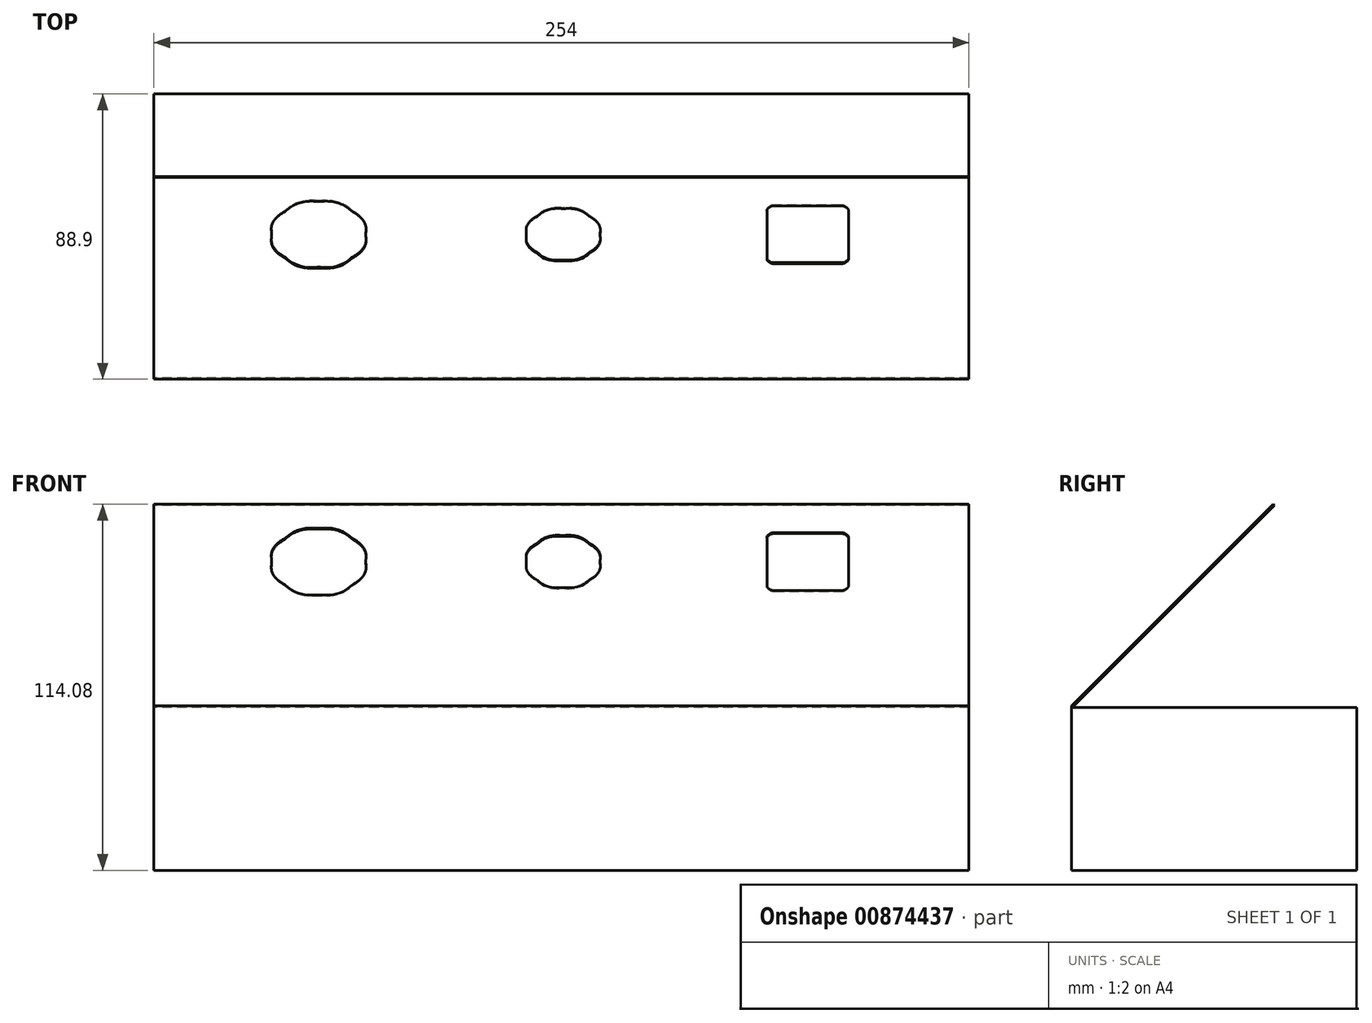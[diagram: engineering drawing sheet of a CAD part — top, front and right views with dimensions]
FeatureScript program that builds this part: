
annotation { "Feature Type Name" : "Feature", "Feature Type Description" : "" }
export const myFeature = defineFeature(function(context is Context, id is Id, definition is map)
    precondition{}
    {
        {
            var Q0;
            Q0=qCreatedBy(makeId("Right.planeOp"),FACE);
            var sketch = newSketch(context, id + "F0", { "sketchPlane" : qUnion([Q0])});
            skLineSegment(sketch, "E0.bottom", {"start": v(0, 0) * mm, "end": v(-88.9, 0) * mm});
            skLineSegment(sketch, "E0.top", {"start": v(0, 50.8) * mm, "end": v(-88.5, 50.8) * mm});
            skLineSegment(sketch, "E0.left", {"start": v(0, 0) * mm, "end": v(0, 50.8) * mm});
            skLineSegment(sketch, "E0.right", {"start": v(-88.9, 0) * mm, "end": v(-88.9, 51.22) * mm});
            skLineSegment(sketch, "E1", {"start": v(-88.9, 51.22) * mm, "end": v(-26.04, 114.08) * mm});
            skLineSegment(sketch, "E2", {"start": v(-26.04, 114.08) * mm, "end": v(-25.75, 113.8) * mm});
            skLineSegment(sketch, "E3", {"start": v(-25.75, 113.8) * mm, "end": v(-88.5, 51.05) * mm});
            skLineSegment(sketch, "E4", {"start": v(-88.5, 50.8) * mm, "end": v(-88.5, 51.05) * mm});
            skLineSegment(sketch, "E5", {"start": v(-88.5, 50.8) * mm, "end": v(-88.9, 50.8) * mm, "construction": true});
            skSolve(sketch);
        }
        {
            var Q0;
            Q0=qSketchRegion(id+"F0",true);
            extrude(context, id + "F1", {"entities" : qUnion([Q0]), "endBound" : BoundingType.SYMMETRIC, "depth" : 254 * mm, "offsetDistance" : 25.4 * mm});
        }
        {
            var Q0;
            Q0=makeQuery(id+"F1.opExtrude","SWEPT_FACE",FACE,{"disambiguationData":[OSD([sQuery(id+"F0.wireOp",EDGE,"E1")])]});
            var sketch = newSketch(context, id + "F2", { "sketchPlane" : qUnion([Q0])});
            skLineSegment(sketch, "E6", {"start": v(89.43, 26.68) * mm, "end": v(89.43, 47.32) * mm});
            skLineSegment(sketch, "E7", {"start": v(87.05, 49.7) * mm, "end": v(66.4, 49.7) * mm});
            skLineSegment(sketch, "E8", {"start": v(66.4, 24.3) * mm, "end": v(87.05, 24.3) * mm});
            skLineSegment(sketch, "E9", {"start": v(64.03, 47.32) * mm, "end": v(64.03, 26.68) * mm});
            skLineSegment(sketch, "E10", {"start": v(127.53, -26.5) * mm, "end": v(127.53, 61.6) * mm, "construction": true});
            skLineSegment(sketch, "E11", {"start": v(-126.47, 61.6) * mm, "end": v(127.53, 61.6) * mm, "construction": true});
            skLineSegment(sketch, "E12", {"start": v(-126.47, -26.5) * mm, "end": v(-126.47, 61.6) * mm, "construction": true});
            skLineSegment(sketch, "E13", {"start": v(127.53, -26.5) * mm, "end": v(-126.47, -26.5) * mm, "construction": true});
            skFitSpline(sketch, "E14", {"points": [v(-75.67, 51.69) * mm, v(-79.52, 51.69) * mm, v(-83.34, 50.1) * mm, v(-86.06, 47.39) * mm]});
            skFitSpline(sketch, "E15", {"points": [v(-86.06, 47.39) * mm, v(-88.77, 44.67) * mm, v(-90.36, 40.85) * mm, v(-90.36, 37) * mm, v(-90.36, 33.16) * mm, v(-88.77, 29.34) * mm, v(-86.06, 26.62) * mm]});
            skFitSpline(sketch, "E16", {"points": [v(-86.06, 26.62) * mm, v(-83.34, 23.9) * mm, v(-79.52, 22.32) * mm, v(-75.67, 22.32) * mm, v(-71.83, 22.32) * mm, v(-68, 23.9) * mm, v(-65.29, 26.62) * mm]});
            skFitSpline(sketch, "E17", {"points": [v(-65.29, 26.62) * mm, v(-62.57, 29.34) * mm, v(-60.99, 33.16) * mm, v(-60.99, 37) * mm, v(-60.99, 40.85) * mm, v(-62.57, 44.67) * mm, v(-65.29, 47.39) * mm]});
            skFitSpline(sketch, "E18", {"points": [v(-65.29, 47.39) * mm, v(-68, 50.1) * mm, v(-71.83, 51.69) * mm, v(-75.67, 51.69) * mm]});
            skFitSpline(sketch, "E19", {"points": [v(89.43, 47.32) * mm, v(89.43, 47.94) * mm, v(89.17, 48.56) * mm, v(88.73, 49) * mm]});
            skFitSpline(sketch, "E20", {"points": [v(88.73, 49) * mm, v(88.29, 49.45) * mm, v(87.67, 49.7) * mm, v(87.05, 49.7) * mm]});
            skFitSpline(sketch, "E21", {"points": [v(87.05, 24.3) * mm, v(87.67, 24.3) * mm, v(88.29, 24.56) * mm, v(88.73, 25) * mm]});
            skFitSpline(sketch, "E22", {"points": [v(88.73, 25) * mm, v(89.17, 25.44) * mm, v(89.43, 26.06) * mm, v(89.43, 26.68) * mm]});
            skFitSpline(sketch, "E23", {"points": [v(64.03, 26.68) * mm, v(64.03, 26.06) * mm, v(64.29, 25.44) * mm, v(64.73, 25) * mm]});
            skFitSpline(sketch, "E24", {"points": [v(64.73, 25) * mm, v(65.17, 24.56) * mm, v(65.79, 24.3) * mm, v(66.4, 24.3) * mm]});
            skFitSpline(sketch, "E25", {"points": [v(66.4, 49.7) * mm, v(65.79, 49.7) * mm, v(65.17, 49.45) * mm, v(64.73, 49) * mm]});
            skFitSpline(sketch, "E26", {"points": [v(64.73, 49) * mm, v(64.29, 48.56) * mm, v(64.03, 47.94) * mm, v(64.03, 47.32) * mm]});
            skFitSpline(sketch, "E27", {"points": [v(0.53, 48.51) * mm, v(-2.49, 48.51) * mm, v(-5.48, 47.27) * mm, v(-7.6, 45.14) * mm]});
            skFitSpline(sketch, "E28", {"points": [v(-7.6, 45.14) * mm, v(-9.74, 43.01) * mm, v(-10.98, 40.02) * mm, v(-10.98, 37) * mm, v(-10.98, 33.99) * mm, v(-9.74, 31) * mm, v(-7.6, 28.86) * mm]});
            skFitSpline(sketch, "E29", {"points": [v(-7.6, 28.86) * mm, v(-5.48, 26.73) * mm, v(-2.49, 25.5) * mm, v(0.53, 25.5) * mm, v(3.54, 25.5) * mm, v(6.54, 26.73) * mm, v(8.67, 28.86) * mm]});
            skFitSpline(sketch, "E30", {"points": [v(8.67, 28.86) * mm, v(10.8, 31) * mm, v(12.04, 33.99) * mm, v(12.04, 37) * mm, v(12.04, 40.02) * mm, v(10.8, 43.01) * mm, v(8.67, 45.14) * mm]});
            skFitSpline(sketch, "E31", {"points": [v(8.67, 45.14) * mm, v(6.54, 47.27) * mm, v(3.54, 48.51) * mm, v(0.53, 48.51) * mm]});
            skFitSpline(sketch, "E32", {"points": [v(0.53, 48.51) * mm, v(-2.49, 48.51) * mm, v(-5.48, 47.27) * mm, v(-7.6, 45.14) * mm]});
            skFitSpline(sketch, "E33", {"points": [v(-7.6, 45.14) * mm, v(-9.74, 43) * mm, v(-10.98, 40.02) * mm, v(-10.98, 37) * mm, v(-10.98, 33.99) * mm, v(-9.74, 31) * mm, v(-7.6, 28.86) * mm]});
            skFitSpline(sketch, "E34", {"points": [v(-7.6, 28.86) * mm, v(-5.48, 26.73) * mm, v(-2.49, 25.5) * mm, v(0.53, 25.5) * mm, v(3.54, 25.5) * mm, v(6.54, 26.73) * mm, v(8.67, 28.86) * mm]});
            skFitSpline(sketch, "E35", {"points": [v(8.67, 28.86) * mm, v(10.8, 31) * mm, v(12.04, 33.99) * mm, v(12.04, 37) * mm, v(12.04, 40.02) * mm, v(10.8, 43) * mm, v(8.67, 45.14) * mm]});
            skFitSpline(sketch, "E36", {"points": [v(8.67, 45.14) * mm, v(6.54, 47.27) * mm, v(3.54, 48.51) * mm, v(0.53, 48.51) * mm]});
            skSolve(sketch);
        }
        {
            var Q0;
            Q0=qSketchRegion(id+"F2",true);
            var Q1;
            Q1=makeQuery(id+"F1.opExtrude","SWEPT_FACE",FACE,{"disambiguationData":[OSD([sQuery(id+"F0.wireOp",EDGE,"E3")])]});
            extrude(context, id + "F3", {"entities" : qUnion([Q0]), "operationType" : NewBodyOperationType.REMOVE, "endBound" : BoundingType.UP_TO_SURFACE, "oppositeDirection" : true, "depth" : 25.4 * mm, "endBoundEntityFace" : qUnion([Q1]), "offsetDistance" : 25.4 * mm});
        }
    });
